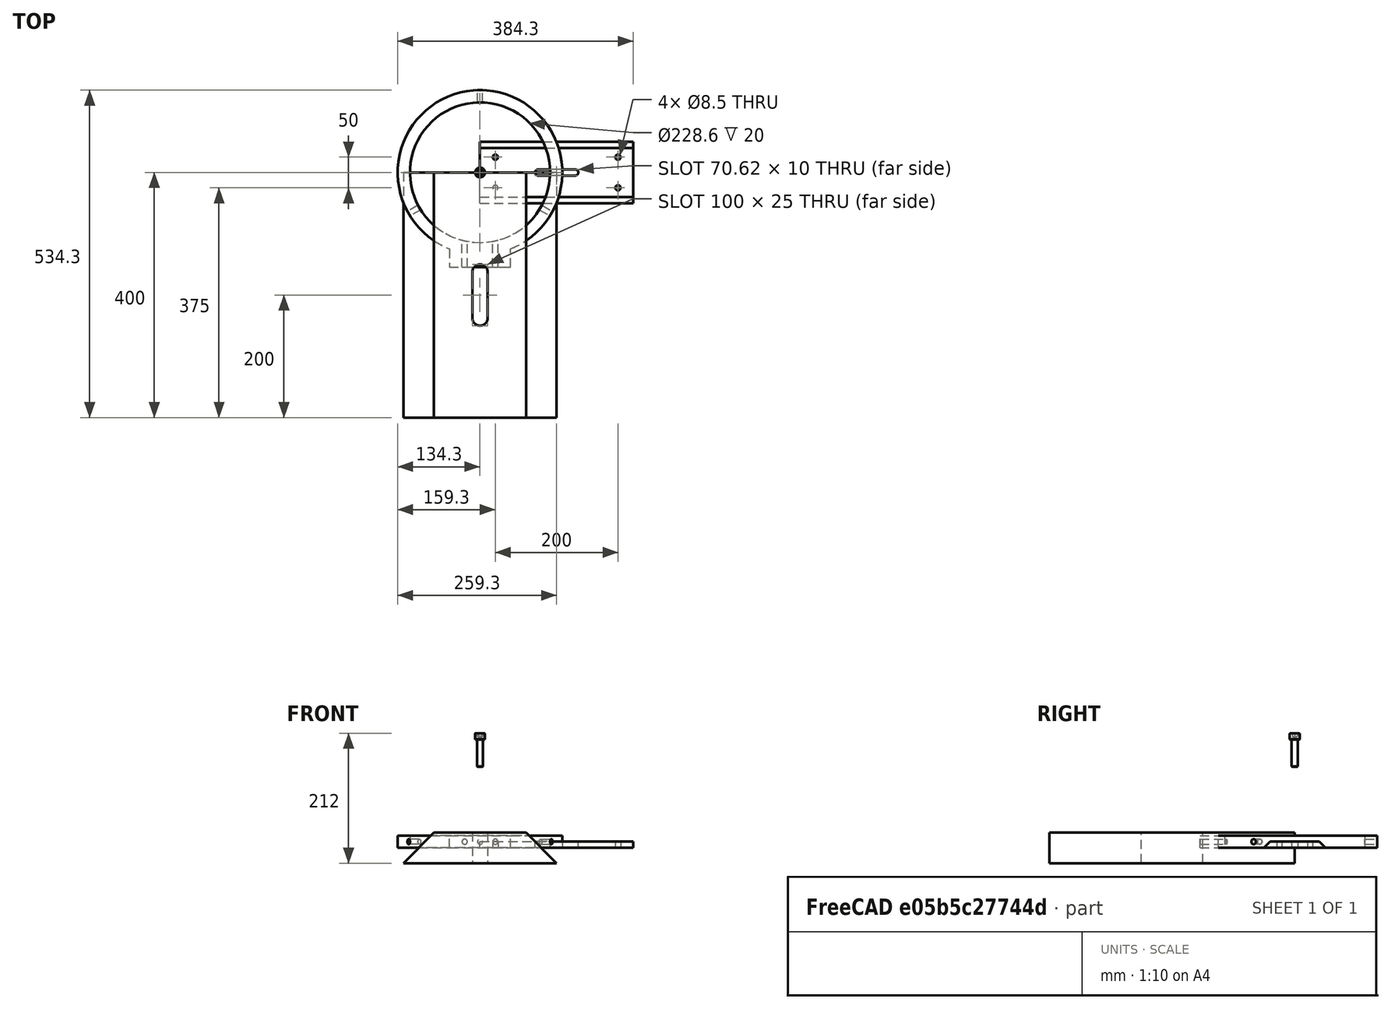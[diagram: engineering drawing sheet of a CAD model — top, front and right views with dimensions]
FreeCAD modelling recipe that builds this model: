
FCSTD DOCUMENT  (FreeCAD 1.0RUnknown)
Label: wedge-2
License: All rights reserved
LicenseURL: https://en.wikipedia.org/wiki/All_rights_reserved
objects: App::Link×13, Sketcher::SketchObject×9, App::FeaturePython×7, PartDesign::Pad×3, PartDesign::Hole×3, PartDesign::Body×3, PartDesign::Pocket×2, Assembly::JointGroup×2, Assembly::AssemblyObject×2, Assembly::AssemblyLink×2, App::Part×2, App::VarSet×1, Part::FeaturePython×1, PartDesign::SubShapeBinder×1, PartDesign::PolarPattern×1
note: 49 computed .brp shape members not serialized (recipe doc carries the construction recipe); baked Part::Feature solids carry a one-line shape summary decoded from their .brp

FEATURE [App::VarSet] VarSet  label="Dimensions"
  BaseWidth = 150
FEATURE [Part::FeaturePython] Screw  label="M10x45-Screw"  # WARN: FeaturePython — macro-defined, semantics opaque (R4)
  Diameter = 9
  Invert = false
  LeftHanded = false
  Length = 6
  LengthCustom = 45
  MatchOuter = false
  OffsetAngle = 0
  Placement = pos=(0,0,177) rot=(0,0,1;0rad)
  Thread = false
  Type = 75
FEATURE [Sketcher::SketchObject] Sketch003
  ArcFitTolerance = 1e-06
  AttachmentSupport = -> [YZ_Plane003]
  FullyConstrained = true
  MakeInternals = false
  MapMode = 5
  Placement = pos=(0,0,0) rot=(0.57735,0.57735,0.57735;2.0944rad)
  sketch-geometry (4):
    g0: LineSegment StartX=-40 StartY=10 StartZ=0 EndX=40 EndY=10 EndZ=0
    g1: LineSegment StartX=-50 StartY=0 StartZ=0 EndX=50 EndY=5e-16 EndZ=0
    g2: LineSegment StartX=-50 StartY=0 StartZ=0 EndX=-40 EndY=10 EndZ=0
    g3: LineSegment StartX=40 StartY=10 StartZ=0 EndX=50 EndY=5e-16 EndZ=0
  constraints (10):
    c: Coincident(g2,g1)
    c: Coincident(g2,g0)
    c: Coincident(g3,g0)
    c: Coincident(g3,g1)
    c: Symmetric(g1,g1,g-2)
    c: Symmetric(g0,g0,g-2)
    c: DistanceX(g1,g1) = 100
    c: Angle(g1,g2) = 0.785398
    c: PointOnObject(g-1,g1)
    c: Distance(g0,g1) = 10
FEATURE [PartDesign::Pad] Pad002
  Direction = (1,0,0)
  Length = 250
  Length2 = 10
  Placement = pos=(0,0,0) rot=(1,1,1;2.0944rad)
  Profile = -> Sketch003
  ReferenceAxis = -> Sketch003 [N_Axis]
  Refine = true
  Suppressed = false
  Type = 0
FEATURE [Sketcher::SketchObject] Sketch004
  ArcFitTolerance = 1e-06
  AttachmentSupport = -> [Pad002]
  ExternalGeometry = -> [Pad002]
  FullyConstrained = false
  MakeInternals = false
  MapMode = 5
  Placement = pos=(0,2.2e-15,10) rot=(0,0,-1;1.5708rad)
  sketch-geometry (10):
    g0: LineSegment [constr] StartX=0 StartY=225 StartZ=0 EndX=1.13e-13 EndY=250 EndZ=0
    g1: LineSegment [constr] StartX=0 StartY=25 StartZ=0 EndX=0 EndY=0 EndZ=0
    g2: LineSegment [constr] StartX=0 StartY=25 StartZ=0 EndX=-25 EndY=25 EndZ=0
    g3: LineSegment [constr] StartX=0 StartY=25 StartZ=0 EndX=25 EndY=25 EndZ=0
    g4: LineSegment [constr] StartX=0 StartY=225 StartZ=0 EndX=-25 EndY=225 EndZ=0
    g5: LineSegment [constr] StartX=0 StartY=225 StartZ=0 EndX=25 EndY=225 EndZ=0
    g6: Circle CenterX=-25 CenterY=25 CenterZ=0 NormalX=0 NormalY=0 NormalZ=1 AngleXU=0 Radius=5.63511
    g7: Circle CenterX=25 CenterY=25 CenterZ=0 NormalX=0 NormalY=0 NormalZ=1 AngleXU=0 Radius=5.63511
    g8: Circle CenterX=25 CenterY=225 CenterZ=0 NormalX=0 NormalY=0 NormalZ=1 AngleXU=0 Radius=5.63511
    g9: Circle CenterX=-25 CenterY=225 CenterZ=0 NormalX=0 NormalY=0 NormalZ=1 AngleXU=0 Radius=5.63511
  constraints (25):
    c: Symmetric(g-3,g-3,g0)
    c: Coincident(g1,g-1)
    c: Equal(g1,g0)
    c: DistanceY(g0,g0) = 25
    c: Coincident(g2,g1)
    c: Horizontal(g2)
    c: Coincident(g3,g1)
    c: Horizontal(g3)
    c: Coincident(g4,g0)
    c: Horizontal(g4)
    c: Coincident(g5,g0)
    c: Horizontal(g5)
    c: Equal(g5,g4)
    c: Equal(g4,g3)
    c: Equal(g3,g2)
    c: PointOnObject(g0,g-2)
    c: Coincident(g6,g2)
    c: Coincident(g7,g3)
    c: Coincident(g8,g5)
    c: Coincident(g9,g4)
    c: Equal(g6,g8)
    c: Equal(g8,g9)
    c: Equal(g9,g7)
    c: DistanceX(g2,g2) = 25
    c: PointOnObject(g1,g-2)
FEATURE [PartDesign::Hole] Hole
  BaseFeature = -> Pad002
  CustomThreadClearance = 0
  Depth = 25
  DepthType = 0
  Diameter = 8.5
  DrillForDepth = false
  DrillPoint = 1
  DrillPointAngle = 118
  HoleCutCountersinkAngle = 90
  HoleCutCustomValues = false
  HoleCutDepth = 0
  HoleCutDiameter = 22.4
  HoleCutType = 0
  ModelThread = false
  Placement = pos=(0,0,0) rot=(1,1,1;2.0944rad)
  Profile = -> Sketch004
  Refine = true
  Suppressed = false
  Tapered = false
  TaperedAngle = 90
  ThreadClass = 0
  ThreadDepth = 25
  ThreadDepthType = 0
  ThreadDirection = 0
  ThreadFit = 0
  ThreadSize = 18
  ThreadType = 1
  Threaded = true
  UseCustomThreadClearance = false
FEATURE [Sketcher::SketchObject] Sketch005
  ArcFitTolerance = 1e-06
  AttachmentSupport = -> [Hole]
  ExternalGeometry = -> [Hole]
  FullyConstrained = false
  MakeInternals = false
  MapMode = 5
  Placement = pos=(0,2.2e-15,10) rot=(0,0,-1;1.5708rad)
  sketch-geometry (6):
    g0: ArcOfCircle CenterX=0 CenterY=155.311 CenterZ=0 NormalX=0 NormalY=0 NormalZ=1 AngleXU=0 Radius=5 StartAngle=2.9e-15 EndAngle=3.14159
    g1: ArcOfCircle CenterX=-3e-16 CenterY=94.6895 CenterZ=0 NormalX=0 NormalY=0 NormalZ=1 AngleXU=0 Radius=5 StartAngle=3.14159 EndAngle=6.28319
    g2: LineSegment StartX=5 StartY=155.311 StartZ=0 EndX=5 EndY=94.6895 EndZ=0
    g3: LineSegment StartX=-5 StartY=155.311 StartZ=0 EndX=-5 EndY=94.6895 EndZ=0
    g4: LineSegment [constr] StartX=0 StartY=0 StartZ=0 EndX=-3e-16 EndY=94.6895 EndZ=0
    g5: LineSegment [constr] StartX=0 StartY=155.311 StartZ=0 EndX=1.781e-13 EndY=250 EndZ=0
  constraints (13):
    c: Tangent(g0,g2) = 1.5708
    c: Tangent(g0,g3) = -1.5708
    c: Tangent(g1,g2) = 1.5708
    c: Tangent(g1,g3) = -1.5708
    c: Equal(g0,g1)
    c: Vertical(g3)
    c: PointOnObject(g0,g-2)
    c: Radius(g0) = 5
    c: Coincident(g4,g-1)
    c: Coincident(g4,g1)
    c: Coincident(g5,g0)
    c: Symmetric(g-3,g-3,g5)
    c: Equal(g5,g4)
FEATURE [PartDesign::Pocket] Pocket002
  BaseFeature = -> Hole
  Direction = (0,0,-1)
  Length = 5
  Length2 = 5
  Placement = pos=(0,0,0) rot=(1,1,1;2.0944rad)
  Profile = -> Sketch005
  ReferenceAxis = -> Sketch005 [N_Axis]
  Refine = true
  Suppressed = false
  Type = 1
FEATURE [PartDesign::Body] Body002  label="Upper Dovetail"
  AllowCompound = false
  Group = -> [Sketch003,Pad002,Sketch004,Hole,Sketch005,Pocket002]
  Origin = -> Origin003
  Tip = -> Pocket002
FEATURE [Sketcher::SketchObject] Sketch006
  ArcFitTolerance = 1e-06
  AttachmentSupport = -> [XY_Plane004]
  FullyConstrained = true
  MakeInternals = false
  MapMode = 5
  sketch-geometry (5):
    g0: ArcOfCircle CenterX=0 CenterY=0 CenterZ=0 NormalX=0 NormalY=0 NormalZ=1 AngleXU=0 Radius=134.3 StartAngle=5.09388 EndAngle=10.6141
    g1: Circle CenterX=0 CenterY=0 CenterZ=0 NormalX=0 NormalY=0 NormalZ=1 AngleXU=0 Radius=114.3
    g2: LineSegment StartX=-50 StartY=-124.645 StartZ=0 EndX=-50 EndY=-154.645 EndZ=0
    g3: LineSegment StartX=-50 StartY=-154.645 StartZ=0 EndX=50 EndY=-154.645 EndZ=0
    g4: LineSegment StartX=50 StartY=-154.645 StartZ=0 EndX=50 EndY=-124.645 EndZ=0
  constraints (14):
    c: Coincident(g0,g-1)
    c: Coincident(g1,g0)
    c: Coincident(g2,g3)
    c: Coincident(g3,g4)
    c: Vertical(g2)
    c: Vertical(g4)
    c: Horizontal(g3)
    c: Coincident(g2,g0)
    c: Coincident(g0,g4)
    c: Equal(g4,g2)
    c: Diameter(g1) = 228.6
    c: Distance(g0,g1) = 20
    c: DistanceX(g3,g3) = 100
    c: DistanceY(g2,g2) = 30
FEATURE [PartDesign::Pad] Pad003
  Direction = (0,0,1)
  Length = 20
  Length2 = 10
  Profile = -> Sketch006
  ReferenceAxis = -> Sketch006 [N_Axis]
  Refine = true
  Suppressed = false
  Type = 0
FEATURE [PartDesign::SubShapeBinder] Binder
  BindCopyOnChange = 0
  BindMode = 0
  ClaimChildren = false
  Context = -> Part [Body003.Binder.]
  Fuse = false
  MakeFace = true
  OffsetFill = false
  OffsetIntersection = false
  OffsetJoinType = 0
  OffsetOpenResult = false
  PartialLoad = false
  Placement = pos=(168,0,0) rot=(1,0,0;1.5708rad)
  Refine = true
  Relative = true
  Support = -> [Body002[Sketch004.]]
  _Version = 2
FEATURE [Sketcher::SketchObject] Sketch007
  ArcFitTolerance = 1e-06
  AttachmentSupport = -> [Pad003]
  ExternalGeometry = -> [Binder,Pad003]
  FullyConstrained = false
  MakeInternals = false
  MapMode = 5
  Placement = pos=(0,-154.645,0) rot=(1,0,0;1.5708rad)
  sketch-geometry (5):
    g0: LineSegment [constr] StartX=193 StartY=25 StartZ=0 EndX=193 EndY=-25 EndZ=0
    g1: Circle CenterX=-25 CenterY=10 CenterZ=0 NormalX=0 NormalY=0 NormalZ=1 AngleXU=0 Radius=5.55482
    g2: Circle CenterX=25 CenterY=10 CenterZ=0 NormalX=0 NormalY=0 NormalZ=1 AngleXU=0 Radius=5.55482
    g3: LineSegment [constr] StartX=-25 StartY=10 StartZ=0 EndX=25 EndY=10 EndZ=0
    g4: GeomPoint [constr] X=-5.2e-15 Y=10 Z=0
  constraints (9):
    c: Coincident(g0,g-3)
    c: Coincident(g0,g-4)
    c: Coincident(g3,g2)
    c: Equal(g3,g0)
    c: Symmetric(g1,g2,g-2)
    c: Equal(g2,g1)
    c: Symmetric(g3,g3,g4)
    c: Symmetric(g-6,g-5,g4)
    c: PointOnObject(g1,g3)
FEATURE [PartDesign::Hole] Hole001
  BaseFeature = -> Pad003
  CustomThreadClearance = 0
  Depth = 75
  DepthType = 0
  Diameter = 8.5
  DrillForDepth = false
  DrillPoint = 1
  DrillPointAngle = 118
  HoleCutCountersinkAngle = 90
  HoleCutCustomValues = false
  HoleCutDepth = 0
  HoleCutDiameter = 6.1
  HoleCutType = 0
  ModelThread = false
  Profile = -> Sketch007
  Refine = true
  Suppressed = false
  Tapered = false
  TaperedAngle = 90
  ThreadClass = 0
  ThreadDepth = 75
  ThreadDepthType = 0
  ThreadDirection = 0
  ThreadFit = 0
  ThreadSize = 18
  ThreadType = 1
  Threaded = true
  UseCustomThreadClearance = false
FEATURE [Sketcher::SketchObject] Sketch008
  ArcFitTolerance = 1e-06
  AttachmentSupport = -> [XZ_Plane004]
  ExternalGeometry = -> [Hole001]
  FullyConstrained = true
  MakeInternals = false
  MapMode = 5
  Placement = pos=(0,0,0) rot=(1,0,0;1.5708rad)
  expr: Constraints[0] = 15 mm
  sketch-geometry (2):
    g0: Circle CenterX=0 CenterY=10 CenterZ=0 NormalX=0 NormalY=0 NormalZ=1 AngleXU=0 Radius=7.5
    g1: GeomPoint [constr] X=0 Y=20 Z=0
  constraints (3):
    c: Diameter(g0) = 15
    c: Symmetric(g-3,g-3,g1)
    c: Symmetric(g-1,g1,g0)
FEATURE [PartDesign::Hole] Hole002
  BaseFeature = -> Hole001
  CustomThreadClearance = 0
  Depth = 200
  DepthType = 0
  Diameter = 8.5
  DrillForDepth = false
  DrillPoint = 1
  DrillPointAngle = 118
  HoleCutCountersinkAngle = 90
  HoleCutCustomValues = false
  HoleCutDepth = 0
  HoleCutDiameter = 0
  HoleCutType = 0
  ModelThread = false
  Profile = -> Sketch008
  Refine = true
  Suppressed = false
  Tapered = false
  TaperedAngle = 90
  ThreadClass = 0
  ThreadDepth = 200
  ThreadDepthType = 0
  ThreadDirection = 0
  ThreadFit = 0
  ThreadSize = 18
  ThreadType = 1
  Threaded = true
  UseCustomThreadClearance = false
FEATURE [PartDesign::PolarPattern] PolarPattern001
  Angle = 240
  Axis = -> Sketch008 [V_Axis]
  BaseFeature = -> Hole002
  Mode = 0
  Occurrences = 3
  Offset = 120
  Originals = -> [Hole002]
  Refine = true
  Suppressed = false
  TransformMode = 0
FEATURE [PartDesign::Body] Body003  label="Saddle Ring 2"
  AllowCompound = false
  Group = -> [Sketch006,Pad003,Sketch007,Binder,Hole001,Sketch008,Hole002,PolarPattern001]
  Origin = -> Origin004
  Tip = -> PolarPattern001
FEATURE [App::Link] Upper_Dovetail  label="Upper Dovetail001"
  LinkedObject = -> Body002
FEATURE [App::FeaturePython] GroundedJoint  # Assembly grounded joint (typed FeaturePython)
  ObjectToGround = -> Upper_Dovetail
FEATURE [App::Link] Saddle_Ring_004  label="Saddle Ring 005"
  LinkPlacement = pos=(0,-0.172898,20.1729) rot=(1,0,0;1.5708rad)
  LinkedObject = -> Body003
  Placement = pos=(0,-0.172898,20.1729) rot=(1,0,0;1.5708rad)
FEATURE [App::FeaturePython] GroundedJoint001  # Assembly grounded joint (typed FeaturePython)
  ObjectToGround = -> Saddle_Ring_004
  Placement = pos=(0,-0.172898,20.1729) rot=(1,0,0;1.5708rad)
FEATURE [App::Link] M10x45_Screw005  label="M10x45-Screw006"
  LinkPlacement = pos=(4e-16,-10.1729,154.436) rot=(0,0,1;3.14159rad)
  LinkedObject = -> Screw
  Placement = pos=(4e-16,-10.1729,154.436) rot=(0,0,1;3.14159rad)
FEATURE [App::Link] M10x45_Screw006  label="M10x45-Screw007"
  LinkPlacement = pos=(0,-2e-16,-46.9588) rot=(1,0,0;3.14159rad)
  LinkedObject = -> Screw
  Placement = pos=(0,-2e-16,-46.9588) rot=(1,0,0;3.14159rad)
FEATURE [App::Link] M10x45_Screw007  label="M10x45-Screw008"
  LinkPlacement = pos=(116.276,-10.1729,-46.9588) rot=(0.866025,0,0.5;3.14159rad)
  LinkedObject = -> Screw
  Placement = pos=(116.276,-10.1729,-46.9588) rot=(0.866025,0,0.5;3.14159rad)
FEATURE [App::FeaturePython] Joint007  label="Slider005"  # Assembly joint (typed FeaturePython)
  Activated = true
  AngleMax = 0
  AngleMin = 0
  Detach1 = false
  Detach2 = false
  Distance = 0
  Distance2 = 0
  EnableAngleMax = false
  EnableAngleMin = false
  EnableLengthMax = true
  EnableLengthMin = false
  JointType = 3 (Slider)
  LengthMax = 35
  LengthMin = 0
  Placement1 = pos=(0,124.263,10) rot=(0,0.707107,-0.707107;3.14159rad)
  Placement2 = pos=(4e-16,1.8e-15,-45) rot=(0,0,1;0rad)
  Reference1 = -> Assembly001 [Saddle_Ring_004.Face7,Saddle_Ring_004.Face7]
  Reference2 = -> Assembly001 [M10x45_Screw005.Face19,M10x45_Screw005.Face19]
FEATURE [App::FeaturePython] Joint008  label="Slider006"  # Assembly joint (typed FeaturePython)
  Activated = true
  AngleMax = 0
  AngleMin = 0
  Detach1 = false
  Detach2 = false
  Distance = 0
  Distance2 = 0
  EnableAngleMax = false
  EnableAngleMin = false
  EnableLengthMax = true
  EnableLengthMin = false
  JointType = 3 (Slider)
  LengthMax = 35
  LengthMin = 0
  Placement1 = pos=(0,-20.1729,-0.172895) rot=(-1,0,0;1.5708rad)
  Placement2 = pos=(0,0,-45) rot=(0,0,1;0rad)
  Reference1 = -> Assembly001 [Saddle_Ring_004.?Face6,Saddle_Ring_004.?Face6]
  Reference2 = -> Assembly001 [M10x45_Screw006.Face19,M10x45_Screw006.Edge1]
FEATURE [App::FeaturePython] Joint009  label="Slider007"  # Assembly joint (typed FeaturePython)
  Activated = true
  AngleMax = 0
  AngleMin = 0
  Detach1 = false
  Detach2 = false
  Distance = 0
  Distance2 = 0
  EnableAngleMax = false
  EnableAngleMin = false
  EnableLengthMax = true
  EnableLengthMin = false
  JointType = 3 (Slider)
  LengthMax = 35
  LengthMin = 0
  Placement1 = pos=(107.615,-62.1317,10) rot=(-0.774597,-0.447214,0.447214;1.82348rad)
  Placement2 = pos=(3.6e-15,-1.8e-15,-45) rot=(0,0,1;0rad)
  Reference1 = -> Assembly001 [Saddle_Ring_004.Face6,Saddle_Ring_004.Face6]
  Reference2 = -> Assembly001 [M10x45_Screw007.Face19,M10x45_Screw007.Face19]
FEATURE [Assembly::JointGroup] Joints001
  Group = -> [GroundedJoint001,Joint007,Joint008,Joint009]
FEATURE [Assembly::AssemblyObject] Assembly001  label="Saddle Ring asm"
  Group = -> [Joints001,Saddle_Ring_004,GroundedJoint001,M10x45_Screw005,M10x45_Screw006,M10x45_Screw007,Joint007,Joint008,Joint009]
  Origin = -> Origin005
  Type = Assembly
FEATURE [App::Link] Saddle_Ring_005  label="Saddle Ring 006"
  LinkPlacement = pos=(0,-0.172898,20.1729) rot=(1,0,0;1.5708rad)
  LinkedObject = -> Saddle_Ring_004
  Placement = pos=(0,-0.172898,20.1729) rot=(1,0,0;1.5708rad)
FEATURE [App::Link] M10x45_Screw008  label="M10x45-Screw009"
  LinkPlacement = pos=(4e-16,-10.1729,154.436) rot=(0,0,1;3.14159rad)
  LinkedObject = -> M10x45_Screw005
  Placement = pos=(4e-16,-10.1729,154.436) rot=(0,0,1;3.14159rad)
FEATURE [App::Link] M10x45_Screw009  label="M10x45-Screw010"
  LinkPlacement = pos=(0,-2e-16,-46.9588) rot=(1,0,0;3.14159rad)
  LinkedObject = -> M10x45_Screw006
  Placement = pos=(0,-2e-16,-46.9588) rot=(1,0,0;3.14159rad)
FEATURE [App::Link] M10x45_Screw010  label="M10x45-Screw011"
  LinkPlacement = pos=(116.276,-10.1729,-46.9588) rot=(0.866025,0,0.5;3.14159rad)
  LinkedObject = -> M10x45_Screw007
  Placement = pos=(116.276,-10.1729,-46.9588) rot=(0.866025,0,0.5;3.14159rad)
FEATURE [Assembly::AssemblyLink] Saddle_Ring_asm  label="Saddle Ring asm001"
  Group = -> [Saddle_Ring_005,M10x45_Screw008,M10x45_Screw009,M10x45_Screw010]
  LinkedObject = -> Assembly001
  Origin = -> Origin006
  Placement = pos=(14.8271,50,144.473) rot=(0,0,1;1.5708rad)
  Rigid = true
FEATURE [App::Link] Saddle_Ring_006  label="Saddle Ring 007"
  LinkPlacement = pos=(0,-0.172898,20.1729) rot=(1,0,0;1.5708rad)
  LinkedObject = -> Saddle_Ring_004
  Placement = pos=(0,-0.172898,20.1729) rot=(1,0,0;1.5708rad)
FEATURE [App::Link] M10x45_Screw011  label="M10x45-Screw012"
  LinkPlacement = pos=(4e-16,-10.1729,154.436) rot=(0,0,1;3.14159rad)
  LinkedObject = -> M10x45_Screw005
  Placement = pos=(4e-16,-10.1729,154.436) rot=(0,0,1;3.14159rad)
FEATURE [App::Link] M10x45_Screw012  label="M10x45-Screw013"
  LinkPlacement = pos=(0,-2e-16,-46.9588) rot=(1,0,0;3.14159rad)
  LinkedObject = -> M10x45_Screw006
  Placement = pos=(0,-2e-16,-46.9588) rot=(1,0,0;3.14159rad)
FEATURE [App::Link] M10x45_Screw013  label="M10x45-Screw014"
  LinkPlacement = pos=(116.276,-10.1729,-46.9588) rot=(0.866025,0,0.5;3.14159rad)
  LinkedObject = -> M10x45_Screw007
  Placement = pos=(116.276,-10.1729,-46.9588) rot=(0.866025,0,0.5;3.14159rad)
FEATURE [Assembly::AssemblyLink] Saddle_Ring_asm001  label="Saddle Ring asm002"
  Group = -> [Saddle_Ring_006,M10x45_Screw011,M10x45_Screw012,M10x45_Screw013]
  LinkedObject = -> Assembly001
  Origin = -> Origin007
  Placement = pos=(214.827,1.05e-13,144.473) rot=(0,0,1;1.5708rad)
  Rigid = true
FEATURE [App::FeaturePython] Joint  label="Fixed"  # Assembly joint (typed FeaturePython)
  Activated = true
  AngleMax = 0
  AngleMin = 0
  Detach1 = false
  Detach2 = false
  Distance = 0
  Distance2 = 0
  EnableAngleMax = false
  EnableAngleMin = false
  EnableLengthMax = false
  EnableLengthMin = false
  JointType = 0 (Fixed)
  LengthMax = 0
  LengthMin = 0
  Placement1 = pos=(-25,-154.645,10) rot=(-1,0,0;1.5708rad)
  Placement2 = pos=(25,25,10) rot=(0,0,1;1.5708rad)
  Reference1 = -> Assembly [Saddle_Ring_asm.Saddle_Ring_005.Face9,Saddle_Ring_asm.Saddle_Ring_005.Edge5]
  Reference2 = -> Assembly [Upper_Dovetail.Edge26,Upper_Dovetail.Edge26]
FEATURE [App::FeaturePython] Joint010  label="Fixed001"  # Assembly joint (typed FeaturePython)
  Activated = true
  AngleMax = 0
  AngleMin = 0
  Detach1 = false
  Detach2 = false
  Distance = 0
  Distance2 = 0
  EnableAngleMax = false
  EnableAngleMin = false
  EnableLengthMax = false
  EnableLengthMin = false
  JointType = 0 (Fixed)
  LengthMax = 0
  LengthMin = 0
  Offset2 = pos=(0,0,0) rot=(0,0,1;3.14159rad)
  Placement1 = pos=(25,-154.645,10) rot=(0,0.707107,-0.707107;3.14159rad)
  Placement2 = pos=(225,25,10) rot=(0,0,1;4.71239rad)
  Reference1 = -> Assembly [Saddle_Ring_asm001.Saddle_Ring_006.Edge25,Saddle_Ring_asm001.Saddle_Ring_006.Edge25]
  Reference2 = -> Assembly [Upper_Dovetail.Edge20,Upper_Dovetail.Edge20]
FEATURE [Assembly::JointGroup] Joints
  Group = -> [GroundedJoint,Joint,Joint010]
FEATURE [Assembly::AssemblyObject] Assembly  label="Saddle asm"
  Group = -> [Joints,Upper_Dovetail,GroundedJoint,Saddle_Ring_asm,Saddle_Ring_asm001,Joint,Joint010]
  Origin = -> Origin002
  Type = Assembly
FEATURE [App::Part] Part  label="Saddle"
  Group = -> [Assembly,Screw,Body002,Body003,Assembly001]
  Origin = -> Origin
FEATURE [Sketcher::SketchObject] Sketch  label="MasterSketch"
  ArcFitTolerance = 1e-06
  FullyConstrained = false
  MakeInternals = false
  sketch-geometry (84):
    g0: Circle CenterX=0 CenterY=0 CenterZ=0 NormalX=0 NormalY=0 NormalZ=1 AngleXU=0 Radius=114.3
    g1: ArcOfCircle CenterX=0 CenterY=0 CenterZ=0 NormalX=0 NormalY=0 NormalZ=1 AngleXU=0 Radius=134.3 StartAngle=5.30491 EndAngle=10.4031
    g2: LineSegment StartX=-75 StartY=-111.407 StartZ=0 EndX=-75 EndY=-154.3 EndZ=0
    g3: LineSegment StartX=-75 StartY=-154.3 StartZ=0 EndX=75 EndY=-154.3 EndZ=0
    g4: LineSegment StartX=75 StartY=-154.3 StartZ=0 EndX=75 EndY=-111.407 EndZ=0
    g5: LineSegment StartX=400 StartY=0 StartZ=0 EndX=550 EndY=0 EndZ=0
    g6: LineSegment StartX=400 StartY=0 StartZ=0 EndX=350 EndY=-50 EndZ=0
    g7: LineSegment StartX=550 StartY=0 StartZ=0 EndX=600 EndY=-50 EndZ=0
    g8: LineSegment StartX=600 StartY=-50 StartZ=0 EndX=350 EndY=-50 EndZ=0
    g9: LineSegment StartX=400 StartY=100 StartZ=0 EndX=550 EndY=100 EndZ=0
    g10: LineSegment StartX=550 StartY=100 StartZ=0 EndX=550 EndY=500 EndZ=0
    g11: LineSegment StartX=550 StartY=500 StartZ=0 EndX=400 EndY=500 EndZ=0
    g12: LineSegment StartX=400 StartY=500 StartZ=0 EndX=400 EndY=170 EndZ=0
    g13: GeomPoint X=475 Y=300 Z=0
    g14: ArcOfCircle CenterX=475 CenterY=337.5 CenterZ=0 NormalX=0 NormalY=0 NormalZ=1 AngleXU=0 Radius=12.5 StartAngle=-9e-16 EndAngle=3.14159
    g15: ArcOfCircle CenterX=475 CenterY=262.5 CenterZ=0 NormalX=0 NormalY=0 NormalZ=1 AngleXU=0 Radius=12.5 StartAngle=3.14159 EndAngle=6.28319
    g16: LineSegment StartX=487.5 StartY=337.5 StartZ=0 EndX=487.5 EndY=262.5 EndZ=0
    g17: LineSegment StartX=462.5 StartY=337.5 StartZ=0 EndX=462.5 EndY=262.5 EndZ=0
    g18: LineSegment [constr] StartX=475 StartY=337.5 StartZ=0 EndX=475 EndY=350 EndZ=0
    g19: LineSegment [constr] StartX=475 StartY=262.5 StartZ=0 EndX=475 EndY=250 EndZ=0
    g20: Circle CenterX=425 CenterY=447.5 CenterZ=0 NormalX=0 NormalY=0 NormalZ=1 AngleXU=0 Radius=12.5
    g21: Circle CenterX=525 CenterY=447.5 CenterZ=0 NormalX=0 NormalY=0 NormalZ=1 AngleXU=0 Radius=12.5
    g22: Circle CenterX=425 CenterY=152.5 CenterZ=0 NormalX=0 NormalY=0 NormalZ=1 AngleXU=0 Radius=12.5
    g23: Circle CenterX=525 CenterY=152.5 CenterZ=0 NormalX=0 NormalY=0 NormalZ=1 AngleXU=0 Radius=12.5
    g24: LineSegment [constr] StartX=425 StartY=447.5 StartZ=0 EndX=525 EndY=447.5 EndZ=0
    g25: LineSegment [constr] StartX=425 StartY=152.5 StartZ=0 EndX=525 EndY=152.5 EndZ=0
    g26: GeomPoint [constr] X=475 Y=447.5 Z=0
    g27: GeomPoint [constr] X=475 Y=152.5 Z=0
    g28: LineSegment [constr] StartX=475 StartY=447.5 StartZ=0 EndX=475 EndY=152.5 EndZ=0
    g29: LineSegment StartX=-400 StartY=0 StartZ=0 EndX=-250 EndY=0 EndZ=0
    g30: LineSegment StartX=-250 StartY=0 StartZ=0 EndX=-250 EndY=-35 EndZ=0
    g31: LineSegment StartX=-250 StartY=-35 StartZ=0 EndX=-400 EndY=-35 EndZ=0
    g32: LineSegment StartX=-400 StartY=-35 StartZ=0 EndX=-400 EndY=0 EndZ=0
    g33: GeomPoint X=-325 Y=-17.5 Z=0
    g34: LineSegment StartX=400 StartY=170 StartZ=0 EndX=400 EndY=135 EndZ=0
    g35: LineSegment [constr] StartX=400 StartY=135 StartZ=0 EndX=550 EndY=135 EndZ=0
    g36: LineSegment StartX=550 StartY=135 StartZ=0 EndX=550 EndY=170 EndZ=0
    g37: LineSegment [constr] StartX=550 StartY=170 StartZ=0 EndX=400 EndY=170 EndZ=0
    g38: LineSegment [constr] StartX=400 StartY=430 StartZ=0 EndX=550 EndY=430 EndZ=0
    g39: LineSegment StartX=550 StartY=430 StartZ=0 EndX=550 EndY=465 EndZ=0
    g40: LineSegment [constr] StartX=550 StartY=465 StartZ=0 EndX=400 EndY=465 EndZ=0
    g41: LineSegment StartX=400 StartY=465 StartZ=0 EndX=400 EndY=430 EndZ=0
    g42: LineSegment [constr] StartX=425 StartY=447.5 StartZ=0 EndX=425 EndY=435 EndZ=0
    g43: LineSegment [constr] StartX=425 StartY=435 StartZ=0 EndX=425 EndY=430 EndZ=0
    g44: LineSegment [constr] StartX=425 StartY=152.5 StartZ=0 EndX=425 EndY=165 EndZ=0
    g45: LineSegment [constr] StartX=425 StartY=165 StartZ=0 EndX=425 EndY=170 EndZ=0
    g46: LineSegment StartX=400 StartY=135 StartZ=0 EndX=400 EndY=100 EndZ=0
    g47: Circle CenterX=-375 CenterY=-17.5 CenterZ=0 NormalX=0 NormalY=0 NormalZ=1 AngleXU=0 Radius=12.5
    g48: Circle CenterX=-275 CenterY=-17.5 CenterZ=0 NormalX=0 NormalY=0 NormalZ=1 AngleXU=0 Radius=12.5
    g49: LineSegment [constr] StartX=-375 StartY=-17.5 StartZ=0 EndX=-275 EndY=-17.5 EndZ=0
    g50: LineSegment StartX=441.9 StartY=-236.437 StartZ=0 EndX=398.509 EndY=-236.437 EndZ=0
    g51: LineSegment StartX=441.9 StartY=-236.437 StartZ=0 EndX=371.531 EndY=-306.805 EndZ=0
    g52: LineSegment StartX=398.509 StartY=-236.437 StartZ=0 EndX=328.14 EndY=-306.805 EndZ=0
    g53: LineSegment StartX=371.531 StartY=-306.805 StartZ=0 EndX=626.08 EndY=-306.805 EndZ=0
    g54: LineSegment StartX=626.08 StartY=-306.805 StartZ=0 EndX=555.712 EndY=-236.437 EndZ=0
    g55: LineSegment StartX=555.712 StartY=-236.437 StartZ=0 EndX=599.103 EndY=-236.437 EndZ=0
    g56: LineSegment StartX=599.103 StartY=-236.437 StartZ=0 EndX=669.471 EndY=-306.805 EndZ=0
    g57: LineSegment StartX=669.471 StartY=-306.805 StartZ=0 EndX=669.471 EndY=-339.725 EndZ=0
    g58: LineSegment StartX=669.471 StartY=-339.725 StartZ=0 EndX=328.14 EndY=-339.725 EndZ=0
    g59: LineSegment StartX=328.14 StartY=-339.725 StartZ=0 EndX=328.14 EndY=-306.805 EndZ=0
    g60: LineSegment [constr] StartX=328.14 StartY=-306.805 StartZ=0 EndX=371.531 EndY=-306.805 EndZ=0
    g61: LineSegment [constr] StartX=328.14 StartY=-339.725 StartZ=0 EndX=328.14 EndY=-236.437 EndZ=0
    g62: LineSegment StartX=0 StartY=-236.437 StartZ=0 EndX=0 EndY=-339.725 EndZ=0
    g63: LineSegment StartX=0 StartY=-339.725 StartZ=0 EndX=219.571 EndY=-339.725 EndZ=0
    g64: LineSegment StartX=219.571 StartY=-339.725 StartZ=0 EndX=219.571 EndY=-236.437 EndZ=0
    g65: LineSegment StartX=219.571 StartY=-236.437 StartZ=0 EndX=0 EndY=-236.437 EndZ=0
    g66: LineSegment [constr] StartX=219.571 StartY=-306.805 StartZ=0 EndX=0 EndY=-306.805 EndZ=0
    g67: LineSegment [constr] StartX=109.786 StartY=-306.805 StartZ=0 EndX=109.786 EndY=-236.437 EndZ=0
    g68: Circle CenterX=54.8928 CenterY=-271.621 CenterZ=0 NormalX=0 NormalY=0 NormalZ=1 AngleXU=0 Radius=13.7397
    g69: Circle CenterX=164.678 CenterY=-271.621 CenterZ=0 NormalX=0 NormalY=0 NormalZ=1 AngleXU=0 Radius=13.7397
    g70: ArcOfCircle CenterX=-714.9 CenterY=-217.615 CenterZ=0 NormalX=0 NormalY=0 NormalZ=1 AngleXU=0 Radius=169.716 StartAngle=4.37885 EndAngle=6.19633
    g71: ArcOfCircle CenterX=-579.523 CenterY=-229.403 CenterZ=0 NormalX=0 NormalY=0 NormalZ=1 AngleXU=0 Radius=33.8264 StartAngle=6.19633 EndAngle=9.33792
    g72: ArcOfCircle CenterX=-759.389 CenterY=-346.016 CenterZ=0 NormalX=0 NormalY=0 NormalZ=1 AngleXU=0 Radius=33.8264 StartAngle=1.23726 EndAngle=4.37885
    g73: ArcOfCircle CenterX=-714.9 CenterY=-217.615 CenterZ=0 NormalX=0 NormalY=0 NormalZ=1 AngleXU=0 Radius=102.063 StartAngle=4.37885 EndAngle=6.19633
    g74: LineSegment StartX=-854.872 StartY=-126.743 StartZ=0 EndX=-853.532 EndY=-176.726 EndZ=0
    g75: LineSegment StartX=-853.532 StartY=-176.726 StartZ=0 EndX=-553.64 EndY=-168.688 EndZ=0
    g76: LineSegment StartX=-553.64 StartY=-168.688 StartZ=0 EndX=-554.98 EndY=-118.706 EndZ=0
    g77: LineSegment StartX=-554.98 StartY=-118.706 StartZ=0 EndX=-854.872 EndY=-126.743 EndZ=0
    g78: Circle CenterX=-1076.13 CenterY=-190.347 CenterZ=0 NormalX=0 NormalY=0 NormalZ=1 AngleXU=0 Radius=17.5
    g79: Circle CenterX=-579.523 CenterY=-229.403 CenterZ=0 NormalX=0 NormalY=0 NormalZ=1 AngleXU=0 Radius=17.5
    g80: LineSegment [constr] StartX=-597.016 StartY=-229.872 StartZ=0 EndX=-562.029 EndY=-228.934 EndZ=0
    g81: LineSegment StartX=-597.016 StartY=-229.872 StartZ=0 EndX=-598.624 EndY=-169.893 EndZ=0
    g82: LineSegment StartX=-562.029 StartY=-228.934 StartZ=0 EndX=-563.636 EndY=-168.956 EndZ=0
    g83: ArcOfCircle [constr] CenterX=-714.9 CenterY=-217.615 CenterZ=0 NormalX=0 NormalY=0 NormalZ=1 AngleXU=0 Radius=135.89 StartAngle=4.54442 EndAngle=6.19633
  constraints (209):
    c: Coincident(g0,g-1)
    c: Diameter(g0) = 228.6  'Saddle Ring Inner Diameter'
    c: Coincident(g1,g0)
    c: Distance(g0,g1) = 20  'Saddle Ring Thickness'
    c: Vertical(g2)
    c: Coincident(g3,g2)
    c: Horizontal(g3)
    c: Coincident(g4,g3)
    c: Vertical(g4)
    c: Equal(g2,g4)
    c: Distance(g1,g3) = 20
    c: Distance(g3,g3) = 150  'SaddleRingBaseWidth'
    c: Coincident(g1,g2)
    c: Coincident(g1,g4)
    c: PointOnObject(g5,g-1)
    c: Horizontal(g5)
    c: Coincident(g6,g5)
    c: Coincident(g7,g5)
    c: Coincident(g8,g7)
    c: Coincident(g8,g6)
    c: Horizontal(g8)
    c: Equal(g6,g7)
    c: Equal(g5,g3)
    c: Angle(g8,g6) = 0.785398  'DoveTailAngle'
    c: DistanceX(g8,g8) = 250  'DovetailInnerBaseWidth'
    c: Coincident(g9,g10)
    c: Coincident(g10,g11)
    c: Coincident(g11,g12)
    c: Coincident(g46,g9)
    c: Horizontal(g9)
    c: Horizontal(g11)
    c: Vertical(g10)
    c: Vertical(g12)
    c: Equal(g9,g5)
    c: DistanceY(g10,g10) = 400  'DoveTailLength'
    c: Vertical(g9,g5)
    c: Symmetric(g11,g9,g13)
    c: Tangent(g14,g16) = 1.5708
    c: Tangent(g14,g17) = -1.5708
    c: Tangent(g15,g16) = 1.5708
    c: Tangent(g15,g17) = -1.5708
    c: Equal(g14,g15)
    c: Symmetric(g14,g15,g13)
    c: Vertical(g14,g15)
    c: Coincident(g18,g14)
    c: PointOnObject(g18,g14)
    c: Vertical(g18)
    c: Coincident(g19,g15)
    c: PointOnObject(g19,g15)
    c: Vertical(g19)
    c: DistanceY(g19,g18) = 100  'DovetailSlotLength'
    c: Diameter(g14) = 25  'DovetailSlotDiameter'
    c: Equal(g23,g22)
    c: Equal(g22,g20)
    c: Equal(g20,g21)
    c: Coincident(g24,g20)
    c: Coincident(g24,g21)
    c: Horizontal(g24)
    c: Coincident(g25,g22)
    c: Coincident(g25,g23)
    c: Symmetric(g24,g24,g26)
    c: Symmetric(g25,g25,g27)
    c: Equal(g25,g24)
    c: Vertical(g27,g26)
    c: Symmetric(g26,g27,g13)
    c: Coincident(g28,g26)
    c: Coincident(g28,g27)
    c: Horizontal(g25)
    c: Coincident(g29,g30)
    c: Coincident(g30,g31)
    c: Coincident(g31,g32)
    c: Coincident(g32,g29)
    c: Horizontal(g29)
    c: Horizontal(g31)
    c: Vertical(g30)
    c: Vertical(g32)
    c: PointOnObject(g29,g-1)
    c: Equal(g29,g3)
    c: Symmetric(g29,g30,g33)
    c: Coincident(g34,g35)
    c: Coincident(g35,g36)
    c: Coincident(g36,g37)
    c: Coincident(g37,g34)
    c: Vertical(g34)
    c: Vertical(g36)
    c: Horizontal(g35)
    c: Horizontal(g37)
    c: Symmetric(g34,g36,g27)
    c: Coincident(g38,g39)
    c: Coincident(g39,g40)
    c: Coincident(g40,g41)
    c: Coincident(g41,g38)
    c: Horizontal(g38)
    c: Horizontal(g40)
    c: Vertical(g39)
    c: Vertical(g41)
    c: PointOnObject(g38,g12)
    c: Symmetric(g39,g38,g26)
    c: Coincident(g42,g20)
    c: PointOnObject(g42,g20)
    c: Vertical(g42)
    c: Coincident(g43,g42)
    c: PointOnObject(g43,g38)
    c: Vertical(g43)
    c: Distance(g43,g43) = 5
    c: Coincident(g44,g22)
    c: PointOnObject(g44,g22)
    c: Vertical(g44)
    c: Coincident(g45,g44)
    c: PointOnObject(g45,g37)
    c: Vertical(g45)
    c: Equal(g45,g43)
    c: DistanceX(g0,g5) = 400
    c: DistanceY(g-1,g9) = 100
    c: Coincident(g12,g34)
    c: Coincident(g46,g34)
    c: Vertical(g46)
    c: Equal(g46,g30)
    c: Equal(g34,g30)
    c: Equal(g48,g47)
    c: Equal(g47,g22)
    c: Coincident(g49,g47)
    c: Coincident(g49,g48)
    c: Horizontal(g49)
    c: Equal(g25,g49)
    c: Symmetric(g47,g48,g33)
    c: DistanceX(g29,g0) = 250
    c: Diameter(g48) = 25
    c: DistanceX(g49,g49) = 100
    c: Horizontal(g50)
    c: Coincident(g51,g50)
    c: Coincident(g52,g50)
    c: Coincident(g53,g51)
    c: Horizontal(g53)
    c: Coincident(g54,g53)
    c: Horizontal(g55)
    c: Coincident(g56,g55)
    c: Coincident(g57,g56)
    c: Vertical(g57)
    c: Coincident(g58,g57)
    c: Horizontal(g58)
    c: Coincident(g59,g58)
    c: Coincident(g59,g52)
    c: Vertical(g59)
    c: Horizontal(g51,g52)
    c: Horizontal(g53,g56)
    c: Equal(g50,g55)
    c: Coincident(g55,g54)
    c: Equal(g54,g51)
    c: Equal(g56,g52)
    c: Angle(g53,g51) = 0.785398
    c: Horizontal(g50,g54)
    c: Coincident(g60,g52)
    c: Coincident(g60,g51)
    c: Equal(g60,g50)
    c: Coincident(g61,g58)
    c: Vertical(g61)
    c: Horizontal(g50,g61)
    c: Coincident(g62,g63)
    c: Coincident(g63,g64)
    c: Coincident(g64,g65)
    c: Coincident(g65,g62)
    c: Vertical(g62)
    c: Vertical(g64)
    c: Horizontal(g63)
    c: Horizontal(g65)
    c: PointOnObject(g62,g-2)
    c: Equal(g64,g61)
    c: Horizontal(g63,g58)
    c: PointOnObject(g66,g64)
    c: PointOnObject(g66,g62)
    c: Horizontal(g66)
    c: Horizontal(g66,g51)
    c: Symmetric(g66,g66,g67)
    c: Symmetric(g65,g65,g67)
    c: Equal(g69,g68)
    c: Symmetric(g62,g67,g68)
    c: Symmetric(g64,g67,g69)
    c: Coincident(g70,g73)
    c: Tangent(g73,g72) = 1.5708
    c: Tangent(g73,g71) = 1.5708
    c: Tangent(g70,g72) = -1.5708
    c: Tangent(g70,g71) = -1.5708
    c: Coincident(g74,g75)
    c: Coincident(g75,g76)
    c: Coincident(g76,g77)
    c: Coincident(g77,g74)
    c: Diameter(g78) = 35
    c: Equal(g79,g78)
    c: PointOnObject(g80,g79)
    c: PointOnObject(g80,g79)
    c: Coincident(g81,g80)
    c: PointOnObject(g81,g75)
    c: Coincident(g82,g80)
    c: PointOnObject(g82,g75)
    c: Perpendicular(g75,g81)
    c: Perpendicular(g75,g82)
    c: Perpendicular(g77,g76)
    c: Perpendicular(g74,g75)
    c: Perpendicular(g77,g74)
    c: Perpendicular(g81,g80)
    c: Distance(g79,g75) = 60
    c: Distance(g74,g76) = 300
    c: Distance(g77,g75) = 50
    c: Distance(g76,g82) = 10
    c: PointOnObject(g79,g80)
    c: Coincident(g83,g70)
    c: Coincident(g83,g71)
    c: Coincident(g71,g79)
FEATURE [Sketcher::SketchObject] Sketch009
  ArcFitTolerance = 1e-06
  AttachmentSupport = -> [XZ_Plane009]
  FullyConstrained = true
  MakeInternals = false
  MapMode = 5
  Placement = pos=(0,0,0) rot=(1,0,0;1.5708rad)
  expr: Constraints[5] = <<MasterSketch>>.Constraints.SaddleRingBaseWidth
  expr: Constraints[6] = <<MasterSketch>>.Constraints.DovetailInnerBaseWidth
  expr: Constraints[7] = <<MasterSketch>>.Constraints.DoveTailAngle
  sketch-geometry (6):
    g0: LineSegment StartX=-75 StartY=25 StartZ=0 EndX=-125 EndY=-25 EndZ=0
    g1: LineSegment StartX=-125 StartY=-25 StartZ=0 EndX=125 EndY=-25 EndZ=0
    g2: LineSegment StartX=125 StartY=-25 StartZ=0 EndX=75 EndY=25 EndZ=0
    g3: LineSegment StartX=75 StartY=25 StartZ=0 EndX=-75 EndY=25 EndZ=0
    g4: GeomPoint X=-5.4e-15 Y=-25 Z=0
    g5: GeomPoint X=5.4e-15 Y=25 Z=0
  constraints (12):
    c: Coincident(g1,g0)
    c: Horizontal(g1)
    c: Coincident(g2,g1)
    c: Coincident(g3,g2)
    c: Coincident(g3,g0)
    c: Distance(g3,g3) = 150
    c: DistanceX(g1,g1) = 250
    c: Angle(g1,g0) = 0.785398
    c: Symmetric(g2,g0,g-2)
    c: Symmetric(g1,g1,g4)
    c: Symmetric(g3,g3,g5)
    c: Symmetric(g5,g4,g-1)
FEATURE [PartDesign::Pad] Pad
  Direction = (0,-1,2e-16)
  Length = 400
  Length2 = 10
  Placement = pos=(0,0,0) rot=(1,0,0;1.5708rad)
  Profile = -> Sketch009
  ReferenceAxis = -> Sketch009 [N_Axis]
  Refine = true
  Suppressed = false
  Type = 0
  expr: Length = <<MasterSketch>>.Constraints.DoveTailLength
FEATURE [Sketcher::SketchObject] Sketch010
  ArcFitTolerance = 1e-06
  AttachmentSupport = -> [Pad]
  ExternalGeometry = -> [Pad]
  FullyConstrained = true
  MakeInternals = false
  MapMode = 5
  Placement = pos=(0,5e-15,25) rot=(0,0,1;3.14159rad)
  expr: Constraints[14] = <<MasterSketch>>.Constraints.DovetailSlotLength
  expr: Constraints[15] = <<MasterSketch>>.Constraints.DovetailSlotDiameter
  sketch-geometry (7):
    g0: GeomPoint X=3.4e-15 Y=200 Z=0
    g1: ArcOfCircle CenterX=3.5e-15 CenterY=237.5 CenterZ=0 NormalX=0 NormalY=0 NormalZ=1 AngleXU=0 Radius=12.5 StartAngle=1.2e-15 EndAngle=3.14159
    g2: ArcOfCircle CenterX=3.2e-15 CenterY=162.5 CenterZ=0 NormalX=0 NormalY=0 NormalZ=1 AngleXU=0 Radius=12.5 StartAngle=3.14159 EndAngle=6.28319
    g3: LineSegment StartX=12.5 StartY=237.5 StartZ=0 EndX=12.5 EndY=162.5 EndZ=0
    g4: LineSegment StartX=-12.5 StartY=237.5 StartZ=0 EndX=-12.5 EndY=162.5 EndZ=0
    g5: LineSegment [constr] StartX=3.5e-15 StartY=237.5 StartZ=0 EndX=3.5e-15 EndY=250 EndZ=0
    g6: LineSegment [constr] StartX=3.2e-15 StartY=162.5 StartZ=0 EndX=3.2e-15 EndY=150 EndZ=0
  constraints (16):
    c: Symmetric(g-3,g-4,g0)
    c: Tangent(g1,g3) = 1.5708
    c: Tangent(g1,g4) = -1.5708
    c: Tangent(g2,g3) = 1.5708
    c: Tangent(g2,g4) = -1.5708
    c: Equal(g1,g2)
    c: Vertical(g3)
    c: Symmetric(g1,g2,g0)
    c: Coincident(g5,g1)
    c: PointOnObject(g5,g1)
    c: Vertical(g5)
    c: Coincident(g6,g2)
    c: PointOnObject(g6,g2)
    c: Vertical(g6)
    c: DistanceY(g6,g5) = 100
    c: Diameter(g1) = 25
FEATURE [PartDesign::Pocket] Pocket
  BaseFeature = -> Pad
  Direction = (0,0,-1)
  Length = 5
  Length2 = 5
  Placement = pos=(0,0,0) rot=(1,0,0;1.5708rad)
  Profile = -> Sketch010
  ReferenceAxis = -> Sketch010 [N_Axis]
  Refine = true
  Suppressed = false
  Type = 2
FEATURE [PartDesign::Body] Body  label="Dovetail Bottom"
  AllowCompound = false
  Group = -> [Sketch009,Pad,Sketch010,Pocket]
  Origin = -> Origin009
  Tip = -> Pocket
FEATURE [App::Part] Part001
  Group = -> [Body]
  Origin = -> Origin008
